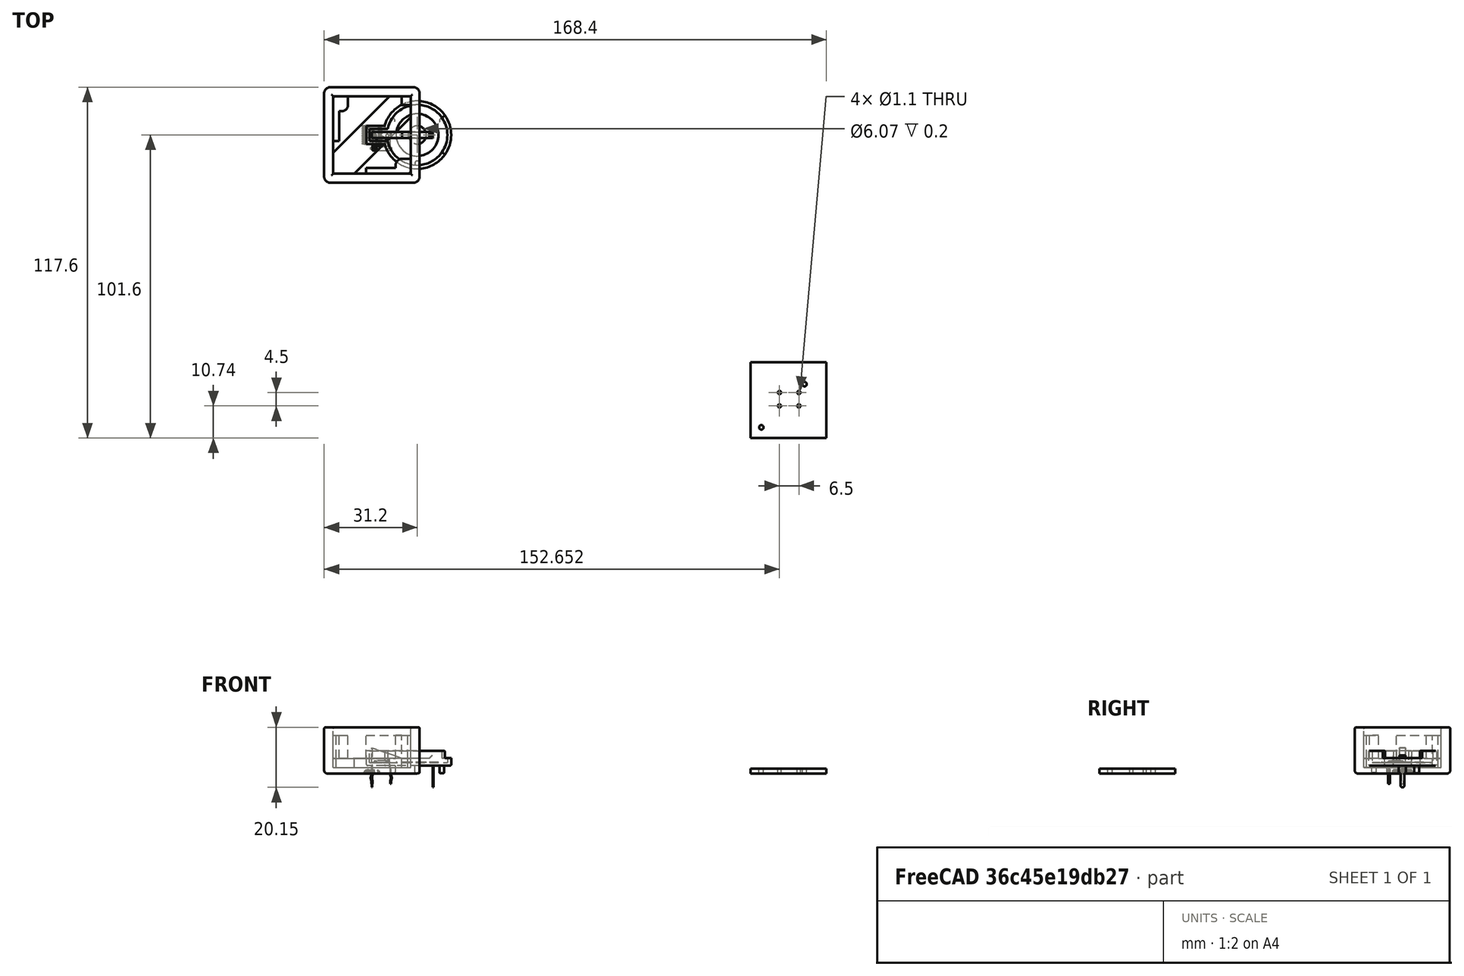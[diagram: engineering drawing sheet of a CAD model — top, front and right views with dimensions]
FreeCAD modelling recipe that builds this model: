
FCSTD DOCUMENT  (FreeCAD 0.18R16131 (Git))
Label: BoxSup
License: All rights reserved
LicenseURL: http://en.wikipedia.org/wiki/All_rights_reserved
objects: Part::Feature×30, App::Part×30, Part::Box×10, Part::Fillet×6, Part::MultiFuse×3, Part::Cut×2, Part::Fuse×2
note: 53 computed .brp shape members not serialized (recipe doc carries the construction recipe); baked Part::Feature solids carry a one-line shape summary decoded from their .brp

FEATURE [Part::Box] Box  label="MainInside"
  AttacherType = Attacher::AttachEngine3D
  Height = 20
  Length = 26
  Placement = pos=(-13,-13,-10) rot=(0,0,1;0rad)
  Width = 26
FEATURE [Part::Feature] Part__Feature  label="SOLID"
  shape: bbox 2 x 1.25 x 1.1 mm, 50 faces (baked)
FEATURE [App::Part] LED_0805_2012Metric
  Group = -> [Part__Feature]
  License = CC BY 3.0
  LicenseURL = http://creativecommons.org/licenses/by/3.0/
  Origin = -> Origin
  Placement = pos=(144.272,-79.248,1.65) rot=(0,0,-1;1.5708rad)
FEATURE [Part::Feature] Part__Feature001  label="SOLID001"
  shape: bbox 7.174 x 6 x 7.8 mm, 105 faces (baked)
FEATURE [App::Part] SW_PUSH_6mm
  Group = -> [Part__Feature001]
  License = CC BY 3.0
  LicenseURL = http://creativecommons.org/licenses/by/3.0/
  Origin = -> Origin001
  Placement = pos=(136.652,-86.36,1.65) rot=(0,0,1;0rad)
FEATURE [Part::Feature] Part__Feature002  label="SOLID002"
  shape: bbox 1.6 x 0.8 x 0.45 mm, 26 faces (baked)
FEATURE [App::Part] R_0603_1608Metric
  Group = -> [Part__Feature002]
  License = CC BY 3.0
  LicenseURL = http://creativecommons.org/licenses/by/3.0/
  Origin = -> Origin002
  Placement = pos=(147.701,-98.679,1.65) rot=(0,0,1;0rad)
FEATURE [Part::Feature] Part__Feature003  label="SOLID003"
  shape: bbox 1.6 x 0.8 x 0.45 mm, 26 faces (baked)
FEATURE [App::Part] R_0603_1608Metric001
  Group = -> [Part__Feature003]
  License = CC BY 3.0
  LicenseURL = http://creativecommons.org/licenses/by/3.0/
  Origin = -> Origin003
  Placement = pos=(145.411,-99.187,1.65) rot=(0,0,1;1.5708rad)
FEATURE [Part::Feature] Part__Feature004  label="SOLID004"
  shape: bbox 6.4 x 6.5 x 1.2 mm, 336 faces (baked)
FEATURE [App::Part] TSSOP_20_4_4x6_5mm_P0_65mm
  Group = -> [Part__Feature004]
  License = CC BY 3.0
  LicenseURL = http://creativecommons.org/licenses/by/3.0/
  Origin = -> Origin004
  Placement = pos=(148.336,-93.81,1.65) rot=(0,0,1;1.5708rad)
FEATURE [Part::Feature] Part__Feature005  label="SOLID005"
  shape: bbox 2 x 1.25 x 1.1 mm, 50 faces (baked)
FEATURE [App::Part] LED_0805_2012Metric001
  Group = -> [Part__Feature005]
  License = CC BY 3.0
  LicenseURL = http://creativecommons.org/licenses/by/3.0/
  Origin = -> Origin005
  Placement = pos=(130.556,-79.248,1.65) rot=(0,0,-1;1.5708rad)
FEATURE [Part::Feature] Part__Feature006  label="SOLID006"
  shape: bbox 2 x 1.25 x 1.1 mm, 50 faces (baked)
FEATURE [App::Part] LED_0805_2012Metric002
  Group = -> [Part__Feature006]
  License = CC BY 3.0
  LicenseURL = http://creativecommons.org/licenses/by/3.0/
  Origin = -> Origin006
  Placement = pos=(135.128,-79.248,1.65) rot=(0,0,-1;1.5708rad)
FEATURE [Part::Feature] Part__Feature007  label="SOLID007"
  shape: bbox 2 x 1.25 x 1.1 mm, 50 faces (baked)
FEATURE [App::Part] LED_0805_2012Metric003
  Group = -> [Part__Feature007]
  License = CC BY 3.0
  LicenseURL = http://creativecommons.org/licenses/by/3.0/
  Origin = -> Origin007
  Placement = pos=(139.7,-79.248,1.65) rot=(0,0,-1;1.5708rad)
FEATURE [Part::Feature] Part__Feature008  label="SOLID008"
  shape: bbox 2 x 1.25 x 1.1 mm, 50 faces (baked)
FEATURE [App::Part] LED_0805_2012Metric004
  Group = -> [Part__Feature008]
  License = CC BY 3.0
  LicenseURL = http://creativecommons.org/licenses/by/3.0/
  Origin = -> Origin008
  Placement = pos=(148.844,-79.248,1.65) rot=(0,0,-1;1.5708rad)
FEATURE [Part::Feature] Part__Feature009  label="SOLID009"
  shape: bbox 1.6 x 0.8 x 0.45 mm, 26 faces (baked)
FEATURE [App::Part] R_0603_1608Metric002
  Group = -> [Part__Feature009]
  License = CC BY 3.0
  LicenseURL = http://creativecommons.org/licenses/by/3.0/
  Origin = -> Origin009
  Placement = pos=(132.588,-79.248,1.65) rot=(0,0,-1;1.5708rad)
FEATURE [Part::Feature] Part__Feature010  label="SOLID010"
  shape: bbox 1.6 x 0.8 x 0.45 mm, 26 faces (baked)
FEATURE [App::Part] R_0603_1608Metric003
  Group = -> [Part__Feature010]
  License = CC BY 3.0
  LicenseURL = http://creativecommons.org/licenses/by/3.0/
  Origin = -> Origin010
  Placement = pos=(137.16,-79.248,1.65) rot=(0,0,-1;1.5708rad)
FEATURE [Part::Feature] Part__Feature011  label="SOLID011"
  shape: bbox 1.6 x 0.8 x 0.45 mm, 26 faces (baked)
FEATURE [App::Part] R_0603_1608Metric004
  Group = -> [Part__Feature011]
  License = CC BY 3.0
  LicenseURL = http://creativecommons.org/licenses/by/3.0/
  Origin = -> Origin011
  Placement = pos=(141.732,-79.248,1.65) rot=(0,0,-1;1.5708rad)
FEATURE [Part::Feature] Part__Feature012  label="SOLID012"
  shape: bbox 1.6 x 0.8 x 0.45 mm, 26 faces (baked)
FEATURE [App::Part] R_0603_1608Metric005
  Group = -> [Part__Feature012]
  License = CC BY 3.0
  LicenseURL = http://creativecommons.org/licenses/by/3.0/
  Origin = -> Origin012
  Placement = pos=(146.304,-79.248,1.65) rot=(0,0,-1;1.5708rad)
FEATURE [Part::Feature] Part__Feature013  label="SOLID013"
  shape: bbox 1.6 x 0.8 x 0.45 mm, 26 faces (baked)
FEATURE [App::Part] R_0603_1608Metric006
  Group = -> [Part__Feature013]
  License = CC BY 3.0
  LicenseURL = http://creativecommons.org/licenses/by/3.0/
  Origin = -> Origin013
  Placement = pos=(150.876,-79.248,1.65) rot=(0,0,-1;1.5708rad)
FEATURE [Part::Feature] Part__Feature014  label="SOLID014"
  shape: bbox 1.6 x 0.8 x 0.8 mm, 28 faces (baked)
FEATURE [App::Part] C_0603_1608Metric
  Group = -> [Part__Feature014]
  License = CC BY 3.0
  LicenseURL = http://creativecommons.org/licenses/by/3.0/
  Origin = -> Origin014
  Placement = pos=(142.494,-94.488,1.65) rot=(0,0,-1;1.5708rad)
FEATURE [Part::Feature] Part__Feature015  label="SOLID015"
  shape: bbox 1.6 x 0.8 x 0.8 mm, 28 faces (baked)
FEATURE [App::Part] C_0603_1608Metric001
  Group = -> [Part__Feature015]
  License = CC BY 3.0
  LicenseURL = http://creativecommons.org/licenses/by/3.0/
  Origin = -> Origin015
  Placement = pos=(143.891,-94.488,1.65) rot=(0,0,-1;1.5708rad)
FEATURE [Part::Feature] Part__Feature016  label="SOLID016"
  shape: bbox 1.6 x 0.8 x 0.8 mm, 28 faces (baked)
FEATURE [App::Part] C_0603_1608Metric002
  Group = -> [Part__Feature016]
  License = CC BY 3.0
  LicenseURL = http://creativecommons.org/licenses/by/3.0/
  Origin = -> Origin016
  Placement = pos=(129.286,-95.631,1.65) rot=(0,0,1;0.785398rad)
FEATURE [Part::Feature] Part__Feature017  label="SOLID017"
  shape: bbox 1.6 x 0.8 x 0.8 mm, 28 faces (baked)
FEATURE [App::Part] C_0603_1608Metric003
  Group = -> [Part__Feature017]
  License = CC BY 3.0
  LicenseURL = http://creativecommons.org/licenses/by/3.0/
  Origin = -> Origin017
  Placement = pos=(128.778,-94.107,1.65) rot=(0,0,1;0.785398rad)
FEATURE [Part::Feature] Part__Feature018  label="SOLID018"
  shape: bbox 29.3 x 24.64 x 13.25 mm, 71 faces (baked)
FEATURE [App::Part] BatteryHolder_Keystone_103_1x20mm
  Group = -> [Part__Feature018]
  License = CC BY 3.0
  LicenseURL = http://creativecommons.org/licenses/by/3.0/
  Origin = -> Origin018
  Placement = pos=(130.556,-98.044,-0.05) rot=(0.92388,0.382683,0;3.14159rad)
FEATURE [Part::Feature] Part__Feature019  label="SOLID019"
  shape: bbox 2.5 x 3 x 1.2 mm, 76 faces (baked)
FEATURE [App::Part] SOT_23
  Group = -> [Part__Feature019]
  License = CC BY 3.0
  LicenseURL = http://creativecommons.org/licenses/by/3.0/
  Origin = -> Origin019
  Placement = pos=(130.81,-88.646,1.65) rot=(0,0,1;0rad)
FEATURE [Part::Feature] Part__Feature020  label="SOLID020"
  shape: bbox 2.5 x 3 x 1.2 mm, 76 faces (baked)
FEATURE [App::Part] SOT_23001
  Group = -> [Part__Feature020]
  License = CC BY 3.0
  LicenseURL = http://creativecommons.org/licenses/by/3.0/
  Origin = -> Origin020
  Placement = pos=(129.286,-85.09,1.65) rot=(0,0,1;3.14159rad)
FEATURE [Part::Feature] Part__Feature021  label="SOLID021"
  shape: bbox 1.6 x 0.8 x 0.45 mm, 26 faces (baked)
FEATURE [App::Part] R_0603_1608Metric007
  Group = -> [Part__Feature021]
  License = CC BY 3.0
  LicenseURL = http://creativecommons.org/licenses/by/3.0/
  Origin = -> Origin021
  Placement = pos=(128.27,-88.8745,1.65) rot=(0,0,1;1.5708rad)
FEATURE [Part::Feature] Part__Feature022  label="SOLID022"
  shape: bbox 1.6 x 0.8 x 0.45 mm, 26 faces (baked)
FEATURE [App::Part] R_0603_1608Metric008
  Group = -> [Part__Feature022]
  License = CC BY 3.0
  LicenseURL = http://creativecommons.org/licenses/by/3.0/
  Origin = -> Origin022
  Placement = pos=(131.699,-85.217,1.65) rot=(0,0,1;1.5708rad)
FEATURE [Part::Feature] Part__Feature023  label="SOLID023"
  shape: bbox 2.5 x 3 x 1.2 mm, 76 faces (baked)
FEATURE [App::Part] SOT_23002
  Group = -> [Part__Feature023]
  License = CC BY 3.0
  LicenseURL = http://creativecommons.org/licenses/by/3.0/
  Origin = -> Origin023
  Placement = pos=(135.89,-97.79,1.65) rot=(0,0,1;1.5708rad)
FEATURE [Part::Feature] Part__Feature024  label="SOLID024"
  shape: bbox 2.5 x 3 x 1.2 mm, 76 faces (baked)
FEATURE [App::Part] SOT_23003
  Group = -> [Part__Feature024]
  License = CC BY 3.0
  LicenseURL = http://creativecommons.org/licenses/by/3.0/
  Origin = -> Origin024
  Placement = pos=(139.446,-97.79,1.65) rot=(0,0,1;1.5708rad)
FEATURE [Part::Feature] Part__Feature025  label="SOLID025"
  shape: bbox 2.5 x 3 x 1.2 mm, 76 faces (baked)
FEATURE [App::Part] SOT_23004
  Group = -> [Part__Feature025]
  License = CC BY 3.0
  LicenseURL = http://creativecommons.org/licenses/by/3.0/
  Origin = -> Origin025
  Placement = pos=(143.002,-97.79,1.65) rot=(0,0,1;0rad)
FEATURE [Part::Feature] Part__Feature026  label="SOLID026"
  shape: bbox 1.6 x 0.8 x 0.45 mm, 26 faces (baked)
FEATURE [App::Part] R_0603_1608Metric009
  Group = -> [Part__Feature026]
  License = CC BY 3.0
  LicenseURL = http://creativecommons.org/licenses/by/3.0/
  Origin = -> Origin026
  Placement = pos=(135.89,-100.33,1.65) rot=(0,0,1;3.14159rad)
FEATURE [Part::Feature] Part__Feature027  label="SOLID027"
  shape: bbox 1.6 x 0.8 x 0.45 mm, 26 faces (baked)
FEATURE [App::Part] R_0603_1608Metric010
  Group = -> [Part__Feature027]
  License = CC BY 3.0
  LicenseURL = http://creativecommons.org/licenses/by/3.0/
  Origin = -> Origin027
  Placement = pos=(133.35,-99.5425,1.65) rot=(0,0,-1;1.5708rad)
FEATURE [Part::Feature] Part__Feature028  label="SOLID028"
  shape: bbox 1.6 x 0.8 x 0.45 mm, 26 faces (baked)
FEATURE [App::Part] R_0603_1608Metric011
  Group = -> [Part__Feature028]
  License = CC BY 3.0
  LicenseURL = http://creativecommons.org/licenses/by/3.0/
  Origin = -> Origin028
  Placement = pos=(139.192,-100.33,1.65) rot=(0,0,1;0rad)
FEATURE [Part::Feature] Part__Feature029  label="COMPOUND"
  shape: bbox 25.4 x 25.4 x 1.6 mm, 12 faces (baked)
FEATURE [App::Part] Open_CASCADE_STEP_translator_6_9_1
  Group = -> [LED_0805_2012Metric,SW_PUSH_6mm,R_0603_1608Metric,R_0603_1608Metric001,TSSOP_20_4_4x6_5mm_P0_65mm,LED_0805_2012Metric001,LED_0805_2012Metric002,LED_0805_2012Metric003,LED_0805_2012Metric004,R_0603_1608Metric002,R_0603_1608Metric003,R_0603_1608Metric004,R_0603_1608Metric005,R_0603_1608Metric006,C_0603_1608Metric,C_0603_1608Metric001,C_0603_1608Metric002,C_0603_1608Metric003,+12 more]
  License = CC BY 3.0
  LicenseURL = http://creativecommons.org/licenses/by/3.0/
  Origin = -> Origin029
  Placement = pos=(-139.7,88.9,12.8) rot=(0,0,1;0rad)
FEATURE [Part::Box] Box012  label="KapakGenis"
  AttacherType = Attacher::AttachEngine3D
  Height = 2
  Length = 32
  Placement = pos=(-16,-16,-12) rot=(0,0,1;0rad)
  Width = 32
FEATURE [Part::Box] Box013  label="KapakIc"
  AttacherType = Attacher::AttachEngine3D
  Height = 3
  Length = 26
  Placement = pos=(-13,-13,-10) rot=(0,0,1;0rad)
  Width = 26
FEATURE [Part::Box] Box014  label="KapakCikinti1"
  AttacherType = Attacher::AttachEngine3D
  Height = 7.8
  Length = 5
  Placement = pos=(-13,8,-7) rot=(0,0,1;0rad)
  Width = 5
FEATURE [Part::Box] Box015  label="KapakCikinti2"
  AttacherType = Attacher::AttachEngine3D
  Height = 7.8
  Length = 5
  Placement = pos=(8,-13,-7) rot=(0,0,1;0rad)
  Width = 5
FEATURE [Part::MultiFuse] Fusion001
  Shapes = -> [Box012,Box013,Box014,Box015]
FEATURE [Part::Fillet] Fillet
  Base = -> Fusion001
  Edges = 2 edges r=2: [Edge43,Edge47]
FEATURE [Part::Fillet] Fillet001
  Base = -> Fillet
  Edges = 2 edges r=1: [Edge38,Edge44]
FEATURE [Part::Fillet] Fillet002
  Base = -> Fillet001
  Edges = 6 edges r=2: [Edge5,Edge38,Edge52,Edge53,Edge56,Edge58]
FEATURE [Part::Box] Box001  label="MainOutside"
  AttacherType = Attacher::AttachEngine3D
  Height = 13.5
  Length = 32
  Placement = pos=(-16,-16,-10) rot=(0,0,1;0rad)
  Width = 32
FEATURE [Part::Cut] Cut
  Base = -> Box001
  Tool = -> Box
FEATURE [Part::Fillet] Fillet003
  Base = -> Cut
  Edges = 4 edges r=2: [Edge1,Edge3,Edge6,Edge15]
FEATURE [Part::Box] Box016  label="Cube"
  AttacherType = Attacher::AttachEngine3D
  Height = 10
  Length = 50
  Placement = pos=(-14.1421,-21.2132,-10) rot=(0,0,1;0.785398rad)
  Width = 10
FEATURE [Part::Cut] Cut001
  Base = -> Fillet002
  Tool = -> Box016
FEATURE [Part::MultiFuse] Fusion
  Placement = pos=(0,0,12) rot=(0,0,1;0rad)
  Shapes = -> [Fillet003,Cut001]
FEATURE [Part::Fillet] Fillet004
  Base = -> Fusion
  Edges = 12 edges r=0.5: [Edge1,Edge6,Edge7,Edge8,Edge9,Edge10,Edge11,Edge12,Edge13,Edge14,Edge15,Edge16]
FEATURE [Part::Fillet] Fillet005
  Base = -> Fillet004
  Edges = 8 edges r=1: [Edge14,Edge20,Edge37,Edge39,Edge40,Edge41,Edge42,Edge43]
FEATURE [Part::Box] Box017  label="Cube001"
  AttacherType = Attacher::AttachEngine3D
  Height = 10.8
  Length = 3
  Placement = pos=(10,10,2) rot=(0,0,1;0rad)
  Width = 3
FEATURE [Part::Box] Box018  label="Cube002"
  AttacherType = Attacher::AttachEngine3D
  Height = 7.8
  Length = 10
  Placement = pos=(-2,-13,5) rot=(0,0,1;0rad)
  Width = 2
FEATURE [Part::Box] Box019  label="Cube003"
  AttacherType = Attacher::AttachEngine3D
  Height = 7.8
  Length = 2
  Placement = pos=(-13,-2,5) rot=(0,0,1;0rad)
  Width = 10
FEATURE [Part::Fuse] Fusion002
  Base = -> Box017
  Tool = -> Box018
FEATURE [Part::Fuse] Fusion003
  Base = -> Box019
  Tool = -> Fusion002
FEATURE [Part::MultiFuse] Fusion004
  Shapes = -> [Fusion003,Fillet005]
